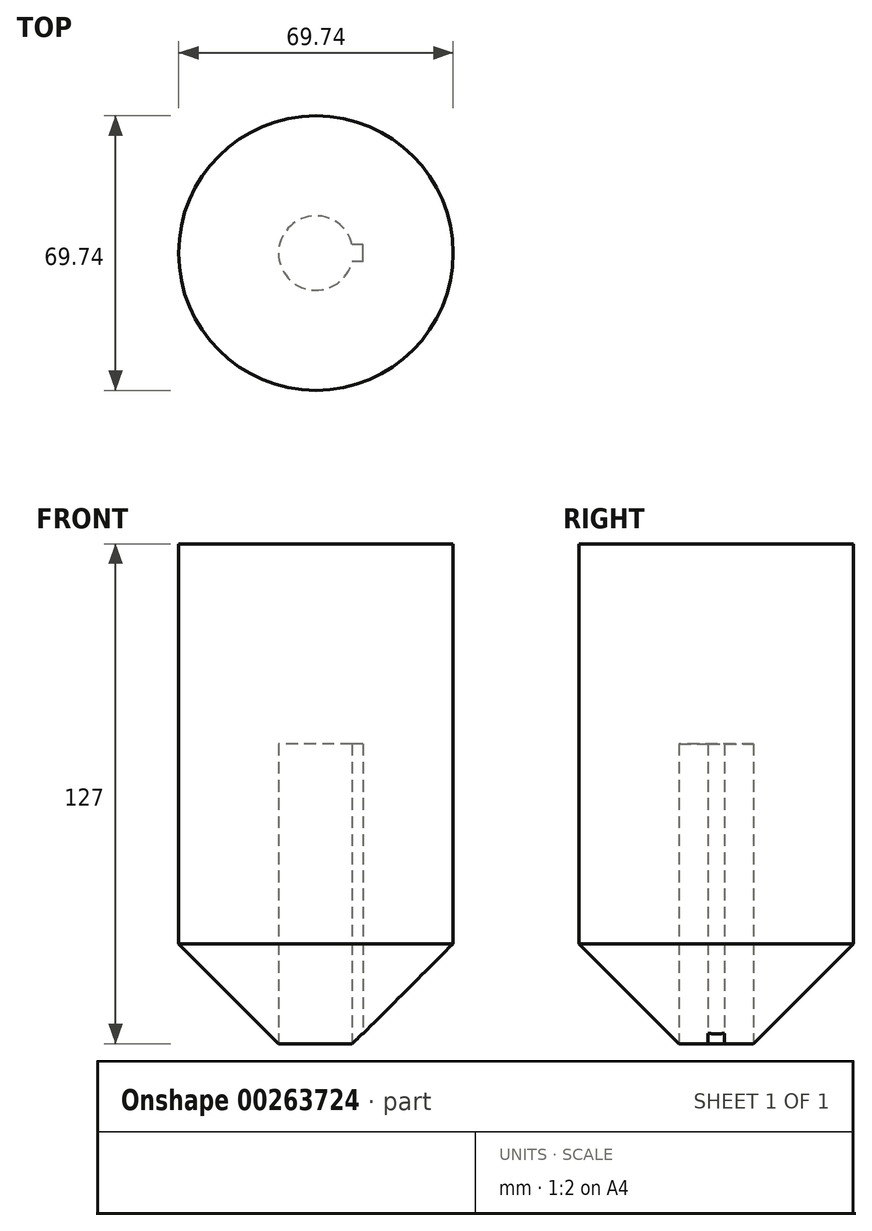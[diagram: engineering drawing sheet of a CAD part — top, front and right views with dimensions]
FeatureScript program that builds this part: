
annotation { "Feature Type Name" : "Feature", "Feature Type Description" : "" }
export const myFeature = defineFeature(function(context is Context, id is Id, definition is map)
    precondition{}
    {
        {
            var Q0;
            Q0=qCreatedBy(makeId("Top.planeOp"),FACE);
            var sketch = newSketch(context, id + "F0", { "sketchPlane" : qUnion([Q0])});
            skCircle(sketch, "E0", {"center": v(0, 0) * mm, "radius": 60.87 * mm});
            skCircle(sketch, "E1", {"center": v(0, 0) * mm, "radius": 35.24 * mm});
            skCircle(sketch, "E2", {"center": v(-31.39, -52.15) * mm, "radius": 2.07 * mm});
            skCircle(sketch, "E3", {"center": v(-31.39, -52.15) * mm, "radius": 2.72 * mm});
            skCircle(sketch, "E4", {"center": v(0, 0) * mm, "radius": 35.63 * mm});
            skCircle(sketch, "E5", {"center": v(0, 0) * mm, "radius": 34.87 * mm});
            skCircle(sketch, "E6", {"center": v(0, 0) * mm, "radius": 35.86 * mm});
            skCircle(sketch, "E7", {"center": v(0, 2.39) * mm, "radius": 38.33 * mm});
            skCircle(sketch, "E8", {"center": v(0, 0) * mm, "radius": 36.1 * mm});
            skCircle(sketch, "E9", {"center": v(0, 0) * mm, "radius": 36.34 * mm});
            skCircle(sketch, "E10", {"center": v(0, 2.39) * mm, "radius": 38.12 * mm});
            skCircle(sketch, "E11", {"center": v(0, 2.39) * mm, "radius": 37.58 * mm});
            skCircle(sketch, "E12", {"center": v(0, 2.39) * mm, "radius": 37.52 * mm});
            skCircle(sketch, "E13", {"center": v(0, 0) * mm, "radius": 39.28 * mm});
            skSolve(sketch);
        }
        {
            var Q0;
            Q0=makeQuery(id+"F0.imprint","IMPRINT",FACE,{"disambiguationData":[TD([[makeQuery(id+"F0.imprint","IMPRINT",EDGE,{"derivedFrom":sQuery(id+"F0.wireOp",EDGE,"E5")}),1.0]])]});
            extrude(context, id + "F1", {"entities" : qUnion([Q0]), "depth" : 127 * mm});
        }
        {
            var Q0;
            Q0=makeQuery(id+"F1.opExtrude","CAP_FACE",FACE,{"disambiguationData":[OSD([sQuery(id+"F0.wireOp",EDGE,"E5")])],"isStart":true});
            chamfer(context, id + "F2", {"entities" : qUnion([Q0]), "width" : 25.4 * mm, "tangentPropagation" : true});
        }
        {
            var Q0;
            Q0=makeQuery(id+"F1.opExtrude","CAP_FACE",FACE,{"disambiguationData":[OSD([sQuery(id+"F0.wireOp",EDGE,"E5")])],"isStart":true});
            var sketch = newSketch(context, id + "F3", { "sketchPlane" : qUnion([Q0])});
            skLineSegment(sketch, "E14.bottom", {"start": v(0, -9.47) * mm, "end": v(0, -9.47) * mm});
            skLineSegment(sketch, "E14.top", {"start": v(0, 9.47) * mm, "end": v(0, 9.47) * mm});
            skLineSegment(sketch, "E14.left", {"start": v(0, -9.47) * mm, "end": v(0, 9.47) * mm});
            skLineSegment(sketch, "E14.right", {"start": v(0, -9.47) * mm, "end": v(0, 9.47) * mm});
            skPoint(sketch, "E14.middle", {"position": v(0, 0) * mm});
            skLineSegment(sketch, "E15.bottom", {"start": v(9.47, 0) * mm, "end": v(-9.47, 0) * mm});
            skLineSegment(sketch, "E15.top", {"start": v(9.47, 0) * mm, "end": v(-9.47, 0) * mm});
            skLineSegment(sketch, "E15.left", {"start": v(9.47, 0) * mm, "end": v(9.47, 0) * mm});
            skLineSegment(sketch, "E15.right", {"start": v(-9.47, 0) * mm, "end": v(-9.47, 0) * mm});
            skLineSegment(sketch, "E16.bottom", {"start": v(7.02, 6.35) * mm, "end": v(-7.02, 6.35) * mm});
            skLineSegment(sketch, "E16.top", {"start": v(7.02, -6.35) * mm, "end": v(-7.02, -6.35) * mm});
            skLineSegment(sketch, "E16.left", {"start": v(7.02, 6.35) * mm, "end": v(7.02, -6.35) * mm});
            skLineSegment(sketch, "E16.right", {"start": v(-7.02, 6.35) * mm, "end": v(-7.02, -6.35) * mm});
            skLineSegment(sketch, "E17.bottom", {"start": v(1.5, 6.35) * mm, "end": v(-1.5, 6.35) * mm});
            skLineSegment(sketch, "E17.top", {"start": v(1.5, -6.35) * mm, "end": v(-1.5, -6.35) * mm});
            skLineSegment(sketch, "E17.left", {"start": v(1.5, 6.35) * mm, "end": v(1.5, -6.35) * mm});
            skLineSegment(sketch, "E17.right", {"start": v(-1.5, 6.35) * mm, "end": v(-1.5, -6.35) * mm});
            skLineSegment(sketch, "E18.bottom", {"start": v(11.94, 2.11) * mm, "end": v(6.99, 2.11) * mm});
            skLineSegment(sketch, "E18.top", {"start": v(11.94, -2.11) * mm, "end": v(6.99, -2.11) * mm});
            skLineSegment(sketch, "E18.left", {"start": v(11.94, 2.11) * mm, "end": v(11.94, -2.11) * mm});
            skLineSegment(sketch, "E18.right", {"start": v(6.99, 2.11) * mm, "end": v(6.99, -2.11) * mm});
            skPoint(sketch, "E18.middle", {"position": v(9.47, 0) * mm});
            skSolve(sketch);
        }
        {
            var Q0;
            {var subQ0=sQuery(id+"F3.wireOp",EDGE,"E16.left");var subQ1=sQuery(id+"F3.wireOp",EDGE,"E15.top");var subQ2=makeQuery(id+"F3.imprint","INTERSECT",VERTEX,{"derivedFrom":[subQ1,subQ0]});Q0=makeQuery(id+"F3.imprint","IMPRINT",FACE,{"disambiguationData":[TD([[makeQuery(id+"F3.imprint","IMPRINT",EDGE,{"disambiguationData":[TD([[subQ2,-1.0]])],"derivedFrom":subQ1}),-1.0]])]});}
            var Q1;
            {var subQ0=sQuery(id+"F3.wireOp",EDGE,"E16.left");var subQ1=sQuery(id+"F3.wireOp",EDGE,"E15.top");var subQ2=makeQuery(id+"F3.imprint","INTERSECT",VERTEX,{"derivedFrom":[subQ1,subQ0]});Q1=makeQuery(id+"F3.imprint","IMPRINT",FACE,{"disambiguationData":[TD([[makeQuery(id+"F3.imprint","IMPRINT",EDGE,{"disambiguationData":[TD([[subQ2,-1.0]])],"derivedFrom":subQ1}),1.0]])]});}
            var Q2;
            {var subQ0=sQuery(id+"F3.wireOp",EDGE,"E16.top");var subQ1=sQuery(id+"F3.wireOp",EDGE,"E14.right");var subQ2=makeQuery(id+"F3.imprint","INTERSECT",VERTEX,{"derivedFrom":[subQ1,subQ0]});Q2=makeQuery(id+"F3.imprint","IMPRINT",FACE,{"disambiguationData":[TD([[makeQuery(id+"F3.imprint","IMPRINT",EDGE,{"disambiguationData":[TD([[subQ2,-1.0]])],"derivedFrom":subQ1}),-1.0]])]});}
            var Q3;
            {var subQ0=sQuery(id+"F3.wireOp",EDGE,"E15.top");var subQ4=sQuery(id+"F3.wireOp",EDGE,"E16.left");var subQ5=makeQuery(id+"F3.imprint","INTERSECT",VERTEX,{"derivedFrom":[subQ0,subQ4]});Q3=makeQuery(id+"F3.imprint","IMPRINT",FACE,{"disambiguationData":[TD([[makeQuery(id+"F3.imprint","IMPRINT",EDGE,{"disambiguationData":[TD([[subQ5,1.0]])],"derivedFrom":subQ4}),1.0]])]});}
            var Q4;
            {var subQ0=sQuery(id+"F3.wireOp",EDGE,"E15.top");var subQ4=sQuery(id+"F3.wireOp",EDGE,"E16.left");var subQ5=makeQuery(id+"F3.imprint","INTERSECT",VERTEX,{"derivedFrom":[subQ0,subQ4]});Q4=makeQuery(id+"F3.imprint","IMPRINT",FACE,{"disambiguationData":[TD([[makeQuery(id+"F3.imprint","IMPRINT",EDGE,{"disambiguationData":[TD([[subQ5,-1.0]])],"derivedFrom":subQ4}),1.0]])]});}
            var Q5;
            {var subQ5=sQuery(id+"F3.wireOp",EDGE,"E18.left");Q5=makeQuery(id+"F3.imprint","IMPRINT",FACE,{"disambiguationData":[TD([[makeQuery(id+"F3.imprint","IMPRINT",EDGE,{"derivedFrom":subQ5}),-1.0]])]});}
            var Q6;
            {var subQ0=sQuery(id+"F3.wireOp",EDGE,"E17.right");var subQ1=sQuery(id+"F3.wireOp",EDGE,"E15.top");var subQ2=makeQuery(id+"F3.imprint","INTERSECT",VERTEX,{"derivedFrom":[subQ1,subQ0]});Q6=makeQuery(id+"F3.imprint","IMPRINT",FACE,{"disambiguationData":[TD([[makeQuery(id+"F3.imprint","IMPRINT",EDGE,{"disambiguationData":[TD([[subQ2,-1.0]])],"derivedFrom":subQ1}),-1.0]])]});}
            var Q7;
            {var subQ0=sQuery(id+"F3.wireOp",EDGE,"E17.right");var subQ1=sQuery(id+"F3.wireOp",EDGE,"E15.top");var subQ2=makeQuery(id+"F3.imprint","INTERSECT",VERTEX,{"derivedFrom":[subQ1,subQ0]});Q7=makeQuery(id+"F3.imprint","IMPRINT",FACE,{"disambiguationData":[TD([[makeQuery(id+"F3.imprint","IMPRINT",EDGE,{"disambiguationData":[TD([[subQ2,-1.0]])],"derivedFrom":subQ1}),1.0]])]});}
            var Q8;
            {var subQ8=sQuery(id+"F3.wireOp",EDGE,"E15.top");var subQ10=sQuery(id+"F3.wireOp",EDGE,"E18.right");var subQ11=makeQuery(id+"F3.imprint","INTERSECT",VERTEX,{"derivedFrom":[subQ8,subQ10]});Q8=makeQuery(id+"F3.imprint","IMPRINT",FACE,{"disambiguationData":[TD([[makeQuery(id+"F3.imprint","IMPRINT",EDGE,{"disambiguationData":[TD([[subQ11,-1.0]])],"derivedFrom":subQ8}),1.0]])]});}
            var Q9;
            {var subQ8=sQuery(id+"F3.wireOp",EDGE,"E18.right");var subQ10=sQuery(id+"F3.wireOp",EDGE,"E15.top");var subQ11=makeQuery(id+"F3.imprint","INTERSECT",VERTEX,{"derivedFrom":[subQ10,subQ8]});Q9=makeQuery(id+"F3.imprint","IMPRINT",FACE,{"disambiguationData":[TD([[makeQuery(id+"F3.imprint","IMPRINT",EDGE,{"disambiguationData":[TD([[subQ11,-1.0]])],"derivedFrom":subQ10}),-1.0]])]});}
            var Q10;
            {var subQ0=sQuery(id+"F3.wireOp",EDGE,"E15.top");var subQ1=sQuery(id+"F3.wireOp",EDGE,"E14.right");var subQ2=makeQuery(id+"F3.imprint","INTERSECT",VERTEX,{"derivedFrom":[subQ1,subQ0]});Q10=makeQuery(id+"F3.imprint","IMPRINT",FACE,{"disambiguationData":[TD([[makeQuery(id+"F3.imprint","IMPRINT",EDGE,{"disambiguationData":[TD([[subQ2,-1.0]])],"derivedFrom":subQ1}),-1.0]])]});}
            var Q11;
            {var subQ0=sQuery(id+"F3.wireOp",EDGE,"E15.top");var subQ1=sQuery(id+"F3.wireOp",EDGE,"E14.right");var subQ2=makeQuery(id+"F3.imprint","INTERSECT",VERTEX,{"derivedFrom":[subQ1,subQ0]});Q11=makeQuery(id+"F3.imprint","IMPRINT",FACE,{"disambiguationData":[TD([[makeQuery(id+"F3.imprint","IMPRINT",EDGE,{"disambiguationData":[TD([[subQ2,-1.0]])],"derivedFrom":subQ1}),1.0]])]});}
            var Q12;
            {var subQ4=sQuery(id+"F3.wireOp",EDGE,"E16.bottom");var subQ7=makeQuery(id+"F3.imprint","INTERSECT",VERTEX,{"derivedFrom":[sQuery(id+"F3.wireOp",EDGE,"E17.right"),subQ4]});Q12=makeQuery(id+"F3.imprint","IMPRINT",FACE,{"disambiguationData":[TD([[makeQuery(id+"F3.imprint","IMPRINT",EDGE,{"disambiguationData":[TD([[subQ7,1.0]])],"derivedFrom":subQ4}),-1.0]])]});}
            var Q13;
            {var subQ0=sQuery(id+"F3.wireOp",EDGE,"E16.top");var subQ1=sQuery(id+"F3.wireOp",EDGE,"E14.right");var subQ2=makeQuery(id+"F3.imprint","INTERSECT",VERTEX,{"derivedFrom":[subQ1,subQ0]});Q13=makeQuery(id+"F3.imprint","IMPRINT",FACE,{"disambiguationData":[TD([[makeQuery(id+"F3.imprint","IMPRINT",EDGE,{"disambiguationData":[TD([[subQ2,-1.0]])],"derivedFrom":subQ1}),1.0]])]});}
            var Q14;
            {var subQ4=sQuery(id+"F3.wireOp",EDGE,"E16.bottom");var subQ6=makeQuery(id+"F3.imprint","INTERSECT",VERTEX,{"derivedFrom":[sQuery(id+"F3.wireOp",EDGE,"E17.left"),subQ4]});Q14=makeQuery(id+"F3.imprint","IMPRINT",FACE,{"disambiguationData":[TD([[makeQuery(id+"F3.imprint","IMPRINT",EDGE,{"disambiguationData":[TD([[subQ6,-1.0]])],"derivedFrom":subQ4}),-1.0]])]});}
            var Q15;
            Q15=makeQuery(id+"F1.opExtrude","CAP_FACE",FACE,{"disambiguationData":[OSD([sQuery(id+"F0.wireOp",EDGE,"E5")])],"isStart":true});
            var Q16;
            Q16=makeQuery(id+"F1.opExtrude","CAP_FACE",FACE,{"disambiguationData":[OSD([sQuery(id+"F0.wireOp",EDGE,"E5")])],"isStart":false});
            var Q17;
            {var subQ4=sQuery(id+"F3.wireOp",EDGE,"E16.top");var subQ6=makeQuery(id+"F3.imprint","INTERSECT",VERTEX,{"derivedFrom":[sQuery(id+"F3.wireOp",EDGE,"E17.left"),subQ4]});Q17=makeQuery(id+"F3.imprint","IMPRINT",FACE,{"disambiguationData":[TD([[makeQuery(id+"F3.imprint","IMPRINT",EDGE,{"disambiguationData":[TD([[subQ6,-1.0]])],"derivedFrom":subQ4}),1.0]])]});}
            extrude(context, id + "F4", {"entities" : qUnion([Q0, Q1, Q2, Q3, Q4, Q5, Q6, Q7, Q8, Q9, Q10, Q11, Q12, Q13, Q14, Q15, Q16, Q17]), "operationType" : NewBodyOperationType.REMOVE, "oppositeDirection" : true, "depth" : 76.2 * mm});
        }
        {
            var Q0;
            Q0=makeQuery(id+"F1.opExtrude","SWEPT_BODY",BODY,{"disambiguationData":[OSD([sQuery(id+"F0.wireOp",EDGE,"E5")])]});
            var Q1;
            Q1=qCreatedBy(makeId("Front.planeOp"),FACE);
            mirror(context, id + "F5", {"operationType" : NewBodyOperationType.ADD, "entities" : qUnion([Q0]), "mirrorPlane" : qUnion([Q1])});
        }
    });
